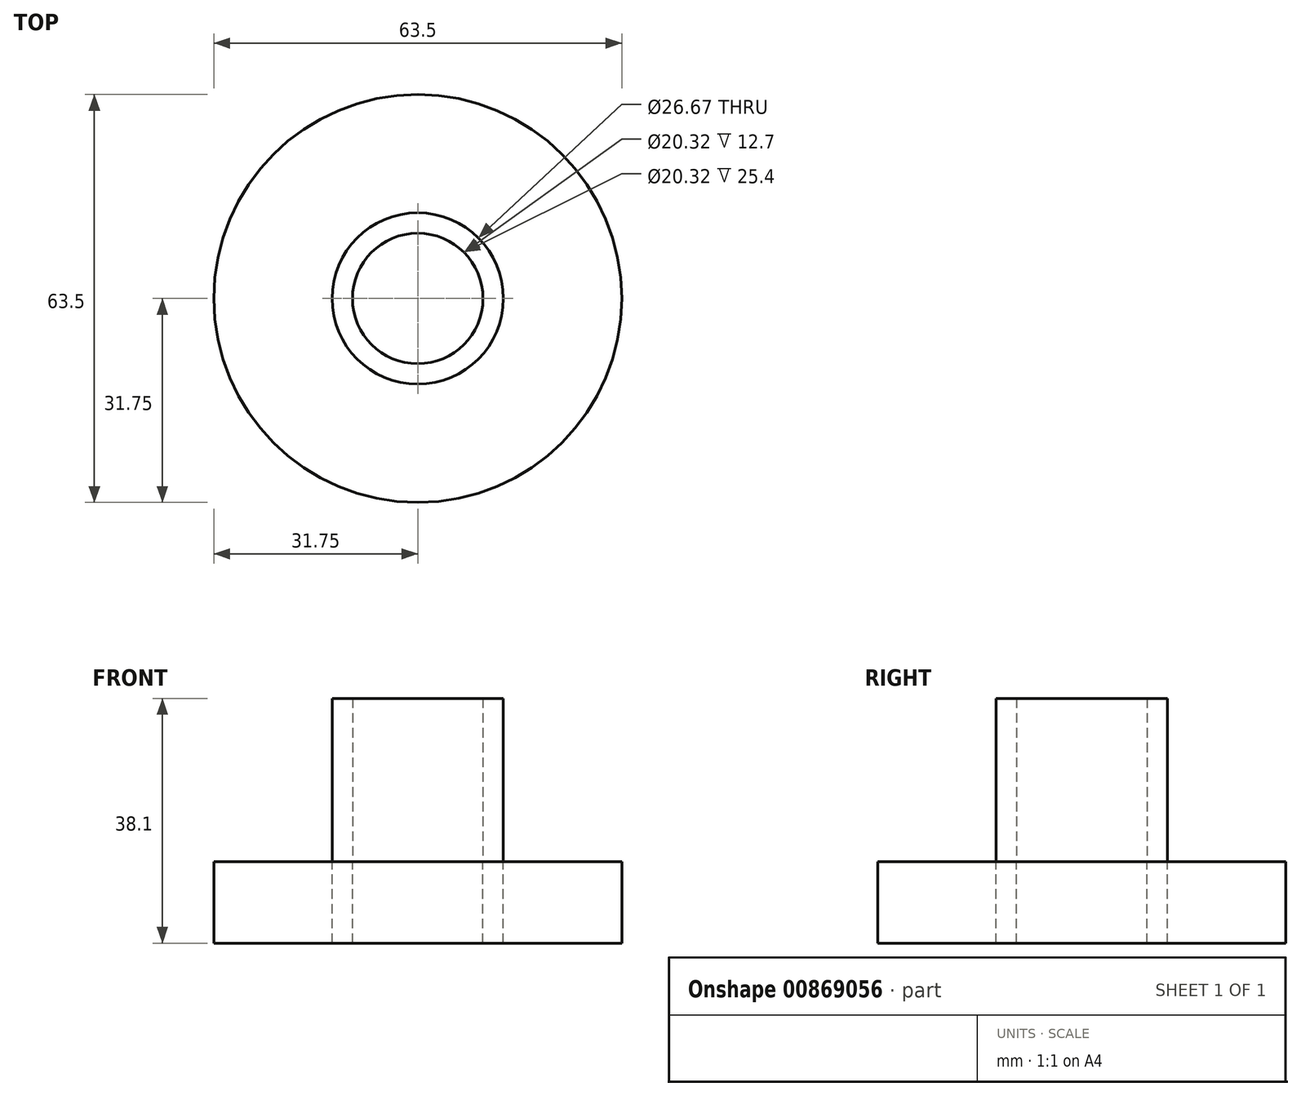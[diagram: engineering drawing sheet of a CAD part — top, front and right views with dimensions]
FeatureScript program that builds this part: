
annotation { "Feature Type Name" : "Feature", "Feature Type Description" : "" }
export const myFeature = defineFeature(function(context is Context, id is Id, definition is map)
    precondition{}
    {
        {
            var Q0;
            Q0=qCreatedBy(makeId("Top.planeOp"),FACE);
            var sketch = newSketch(context, id + "F0", { "sketchPlane" : qUnion([Q0])});
            skCircle(sketch, "E0", {"center": v(0, 0) * mm, "radius": 31.75 * mm});
            skCircle(sketch, "E1", {"center": v(0, 0) * mm, "radius": 10.16 * mm});
            skCircle(sketch, "E2", {"center": v(0, 0) * mm, "radius": 13.34 * mm});
            skSolve(sketch);
        }
        {
            var Q0;
            Q0=makeQuery(id+"F0.imprint","IMPRINT",FACE,{"disambiguationData":[TD([[makeQuery(id+"F0.imprint","IMPRINT",EDGE,{"derivedFrom":sQuery(id+"F0.wireOp",EDGE,"E1")}),-1.0]])]});
            extrude(context, id + "F1", {"entities" : qUnion([Q0]), "depth" : 25.4 * mm, "offsetDistance" : 25.4 * mm});
        }
        {
            var Q0;
            Q0=makeQuery(id+"F0.imprint","IMPRINT",FACE,{"disambiguationData":[TD([[makeQuery(id+"F0.imprint","IMPRINT",EDGE,{"derivedFrom":sQuery(id+"F0.wireOp",EDGE,"E0")}),1.0]])]});
            extrude(context, id + "F2", {"entities" : qUnion([Q0]), "oppositeDirection" : true, "depth" : 12.7 * mm, "offsetDistance" : 25.4 * mm});
        }
        {
            var Q0;
            Q0=makeQuery(id+"F1.opExtrude","CAP_FACE",FACE,{"disambiguationData":[OSD([sQuery(id+"F0.wireOp",EDGE,"E1"),sQuery(id+"F0.wireOp",EDGE,"E2")])],"isStart":true});
            var Q1;
            Q1=makeQuery(id+"F2.opExtrude","CAP_FACE",FACE,{"disambiguationData":[OSD([sQuery(id+"F0.wireOp",EDGE,"E0"),sQuery(id+"F0.wireOp",EDGE,"E2")])],"isStart":false});
            extrude(context, id + "F3", {"entities" : qUnion([Q0]), "endBound" : BoundingType.UP_TO_SURFACE, "depth" : 25.4 * mm, "endBoundEntityFace" : qUnion([Q1]), "offsetDistance" : 25.4 * mm});
        }
    });
